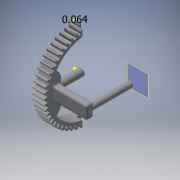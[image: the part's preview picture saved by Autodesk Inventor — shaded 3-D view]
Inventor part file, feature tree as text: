
AUTODESK INVENTOR PART (.ipt)
format: ipt  version: 2018 (Build 220112000, 112)  size: 957,952 bytes
history: native  units: in
note: dims shown in document units (in); Inventor stores cm internally (conversion verified against a paired STEP export)
features: extrude x13, sketch x11, other x6, plane x6, fillet x5, reference x2, projected_geometry x1
ambient origin geometry x8: Origin, YZ Plane, XZ Plane, XY Plane, X Axis, Y Axis, Z Axis, Center Point
bodies: Body1 (feature_tree)
feature tree (44):
  other  "main sketch"
  extrude  "teeth extrude"  Depth=3.25in
  extrude  "other teeth extrude"  Depth=1.2025in
  other  "axel work plane"
  extrude  "axel extrude"  Depth=0.5in TaperAngle=0.0deg
  plane  "Work Plane7"
  extrude  "Extrusion15"  Depth=0.24in
  sketch  "Sketch10"  dims[d13=20.4724in d15=360.0deg d19=0.5in d20=0.0in]
  extrude  "Extrusion16"  Depth=0.311in
  plane  "Work Plane9"
  extrude  "Extrusion18"  Depth=0.0025in
  plane  "Work Plane8"
  extrude  "Extrusion19"  Depth=0.1969in
  extrude  "Extrusion20"  Depth=0.3937in TaperAngle=0.0deg
  extrude  "Extrusion22"  Depth=3.937in TaperAngle=0.0deg
  extrude  "Extrusion23"  Depth=0.29in
  plane  "Work Plane10"
  extrude  "Extrusion26"  Depth=0.0787in TaperAngle=0.0deg
  sketch  "Sketch20"  dims[d97=0.315in d98=0.29in]
  plane  "Work Plane11"
  extrude  "Extrusion28"  Depth=0.0787in TaperAngle=0.0deg
  extrude  "Extrusion29"  Depth=0.0787in
  plane  "Work Plane12"
  fillet  "Fillet8"  Radius=0.3937in
  fillet  "Fillet9"  Radius=0.1489in
  fillet  "Fillet10"  Radius=0.3937in
  fillet  "Fillet11"  Radius=0.0787in
  fillet  "Fillet13"  Radius=0.0787in
  sketch  "Sketch7"  dims[d0=3.0in d1=3.25in]
  sketch  "Sketch9"  dims[d7=1.2025in d8=1.2025in]
  sketch  "Sketch11"  dims[d23=0.5in d24=0.0in d65=0.24in]
  sketch  "Sketch12"  dims[d66=1.3in d67=0.0in d70=0.311in]
  sketch  "Sketch13"  dims[d71=1.4774in d72=0.0in d73=0.0025in]
  sketch  "Sketch15"  dims[d74=1.4774in d75=0.0in d78=0.1969in d79=0.25in]
  sketch  "Sketch16"  dims[d80=39.3701in d81=0.1969in d82=0.0in d83=0.0in d84=0.3937in d85=0.0in]
  sketch  "Sketch19"  dims[d86=3.937in d87=0.0in d93=3.937in d94=0.0in]
  reference  "Reference2"
  sketch  "Sketch21"  dims[d99=0.6299in d100=2.0in d101=0.0in d107=0.75in d108=0.0in d115=0.25in d116=0.3937in d117=0.0in d118=0.1489in d119=0.3937in d120=0.0in d127=0.0787in d128=0.0787in d129=0.0787in d130=0.0787in d132=0.0787in]
  projected_geometry  "Projected Loop1"
  reference  "Reference3"
  other  "<userpath>\OneDrive\Documents\Inventor\TSA\2018\Animatronics\Tortoise\TurtleAssembly.iam"
  other  "TurtleAssembly.iam"
  other  "servo (2):2"
  other  "wheelframe:1"
